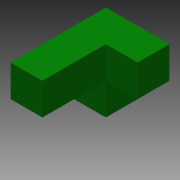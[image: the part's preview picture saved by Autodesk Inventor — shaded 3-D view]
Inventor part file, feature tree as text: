
AUTODESK INVENTOR PART (.ipt)
format: ipt  version: 2015 (Build 190159000, 159)  size: 102,912 bytes
history: native  units: in
note: dims shown in document units (in); Inventor stores cm internally (conversion verified against a paired STEP export)
features: extrude x2, sketch x2
ambient origin geometry x8: Origin, YZ Plane, XZ Plane, XY Plane, X Axis, Y Axis, Z Axis, Center Point
bodies: Solid1 (feature_tree)
feature tree (4):
  extrude  "Extrusion1"  Depth=1.5in
  extrude  "Extrusion2"  Depth=0.75in
  sketch  "Sketch1"  dims[d0=2.25in d1=1.5in]
  sketch  "Sketch2"  dims[d2=0.75in d3=0.75in d4=1.5in d5=0.75in d6=0.75in d7=0.0in d8=0.75in d9=0.0in]
